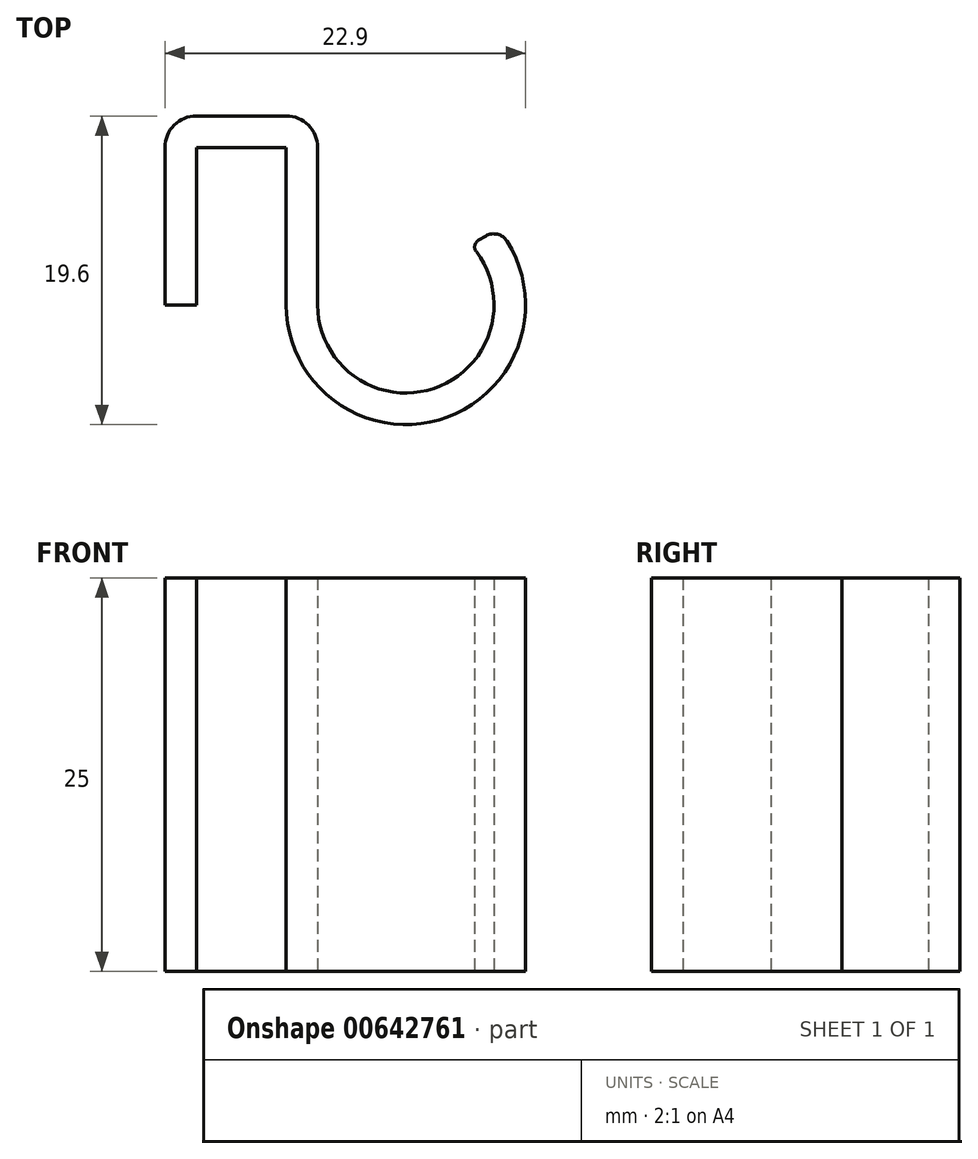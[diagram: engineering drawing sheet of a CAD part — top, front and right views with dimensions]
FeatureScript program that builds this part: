
annotation { "Feature Type Name" : "Feature", "Feature Type Description" : "" }
export const myFeature = defineFeature(function(context is Context, id is Id, definition is map)
    precondition{}
    {
        {
            var Q0;
            Q0=qCreatedBy(makeId("Top.planeOp"),FACE);
            var sketch = newSketch(context, id + "F0", { "sketchPlane" : qUnion([Q0])});
            skLineSegment(sketch, "E0", {"start": v(-2, 12) * mm, "end": v(7.7, 12) * mm});
            skLineSegment(sketch, "E1", {"start": v(7.7, 12) * mm, "end": v(7.7, 0) * mm});
            skLineSegment(sketch, "E2.0", {"start": v(0, 10) * mm, "end": v(5.7, 10) * mm});
            skLineSegment(sketch, "E3", {"start": v(5.7, 0) * mm, "end": v(5.7, 10) * mm});
            skArc(sketch, "E4", {"start": v(7.7, 0) * mm, "mid": v(15.34, -5.21) * mm, "end": v(17.41, 3.8) * mm});
            skArc(sketch, "E5", {"start": v(5.7, 0) * mm, "mid": v(15.87, -7.15) * mm, "end": v(19.17, 4.83) * mm});
            skLineSegment(sketch, "E6", {"start": v(-2, 12) * mm, "end": v(-2, 0) * mm});
            skLineSegment(sketch, "E7", {"start": v(-2, 0) * mm, "end": v(0, 0) * mm});
            skLineSegment(sketch, "E8", {"start": v(0, 0) * mm, "end": v(0, 10) * mm});
            skLineSegment(sketch, "E9", {"start": v(17.41, 3.8) * mm, "end": v(19.17, 4.83) * mm});
            skSolve(sketch);
        }
        {
            var Q0;
            Q0=makeQuery(id+"F0.imprint","IMPRINT",FACE,{"disambiguationData":[TD([[makeQuery(id+"F0.imprint","IMPRINT",EDGE,{"derivedFrom":sQuery(id+"F0.wireOp",EDGE,"E0")}),-1.0]])]});
            extrude(context, id + "F1", {"entities" : qUnion([Q0]), "depth" : 25 * mm, "offsetDistance" : 25 * mm});
        }
        {
            var Q0;
            Q0=makeQuery(id+"F1.opExtrude","SWEPT_EDGE",EDGE,{"disambiguationData":[OSD([sQuery(id+"F0.wireOp",EDGE,"E0"),sQuery(id+"F0.wireOp",EDGE,"E1")])]});
            fillet(context, id + "F2", {"entities" : qUnion([Q0]), "radius" : 2 * mm, "tangentPropagation" : true, "allowEdgeOverflow" : false});
        }
        {
            var Q0;
            Q0=makeQuery(id+"F1.opExtrude","SWEPT_EDGE",EDGE,{"disambiguationData":[OSD([sQuery(id+"F0.wireOp",EDGE,"E0"),sQuery(id+"F0.wireOp",EDGE,"E6")])]});
            fillet(context, id + "F3", {"entities" : qUnion([Q0]), "radius" : 2 * mm, "tangentPropagation" : true, "allowEdgeOverflow" : false});
        }
        {
            var Q0;
            Q0=makeQuery(id+"F1.opExtrude","SWEPT_EDGE",EDGE,{"disambiguationData":[OSD([sQuery(id+"F0.wireOp",EDGE,"E5"),sQuery(id+"F0.wireOp",EDGE,"E9")])]});
            fillet(context, id + "F4", {"entities" : qUnion([Q0]), "radius" : 1 * mm, "tangentPropagation" : true, "allowEdgeOverflow" : false});
        }
        {
            var Q0;
            Q0=makeQuery(id+"F1.opExtrude","SWEPT_EDGE",EDGE,{"disambiguationData":[OSD([sQuery(id+"F0.wireOp",EDGE,"E4"),sQuery(id+"F0.wireOp",EDGE,"E9")])]});
            fillet(context, id + "F5", {"entities" : qUnion([Q0]), "radius" : 0.5 * mm, "tangentPropagation" : true, "allowEdgeOverflow" : false});
        }
    });
